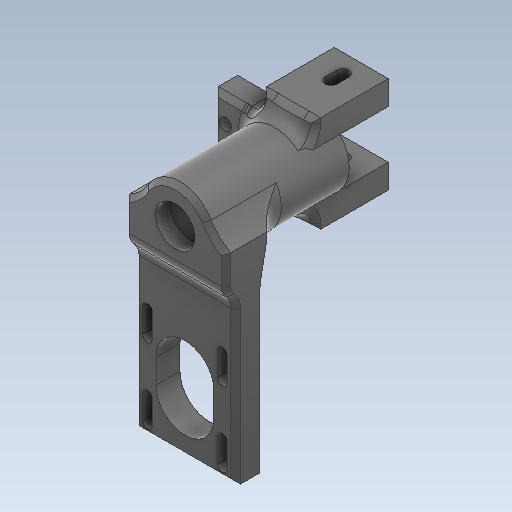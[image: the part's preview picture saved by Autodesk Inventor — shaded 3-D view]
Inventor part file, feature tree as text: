
AUTODESK INVENTOR PART (.ipt)
format: ipt  version: 2020 (Build 240168000, 168)  size: 693,760 bytes
history: native  units: mm
features: extrude x8, sketch x6, fillet x4, chamfer x4, direct_edit x2, projected_geometry x2, move_body x2, hole x1, mirror x1
ambient origin geometry x8: Origin, YZ Plane, XZ Plane, XY Plane, X Axis, Y Axis, Z Axis, Center Point
bodies: Solid1 (feature_tree)
feature tree (30):
  extrude  "Extrusion1"  Depth=57.0mm TaperAngle=0.0deg
  extrude  "Extrusion2"  Depth=5.2mm TaperAngle=0.0deg
  extrude  "Extrusion3"  Depth=10.0mm
  extrude  "Extrusion5"  Depth=20.0mm
  hole  "Hole1"  [1 undecoded]
  direct_edit  "Direct Edit1"
  fillet  "Fillet1"  Radius=5.0mm
  chamfer  "Chamfer1"  [1 undecoded]
  extrude  "Extrusion6"  Depth=10.0mm
  extrude  "Extrusion7"  Depth=10.0mm
  chamfer  "Chamfer2"  Distance=2.0mm Angle=45.0deg
  fillet  "Fillet2"  Radius=42.0mm
  fillet  "Fillet3"  Radius=65.0mm
  extrude  "Extrusion8"  Depth=10.0mm TaperAngle=0.0deg
  chamfer  "Chamfer3"  Distance=4.0mm
  extrude  "Extrusion9"  TaperAngle=0.0deg  [1 undecoded]
  fillet  "Fillet4"  Radius=4.0mm
  chamfer  "Chamfer4"  Distance=7.0mm
  direct_edit  "Direct Edit2"
  mirror  "Mirror2"
  sketch  "Sketch1"  dims[d0=30.0mm d1=57.0mm d2=0.0mm]
  sketch  "Sketch2"  dims[d3=16.3mm d4=5.2mm d5=0.0mm]
  sketch  "Sketch3"  dims[d8=10.0mm d9=10.0mm]
  sketch  "Sketch8"  dims[d10=40.0mm d11=0.0mm d16=20.0mm]
  projected_geometry  "Projected Loop4"
  sketch  "Sketch9"  dims[d17=17.0mm d18=10.0mm d19=0.0mm d20=5.0mm]
  projected_geometry  "Projected Loop5"
  sketch  "Sketch12"  dims[d21=5.0mm d22=5.0mm d23=6.0mm d24=4.0mm d25=2.0mm d26=90.0deg d27=8.0mm d28=20.594885mm d29=0.0mm d30=0.0mm d31=-10.0mm d32=20.0mm d33=6.0mm d34=2.0mm d35=2.0mm d36=45.0deg d37=42.0mm d39=65.0mm d40=13.9mm d41=0.0mm d42=4.0mm d43=0.0mm d44=0.0mm d45=4.0mm d46=2.0mm d47=45.0deg d48=7.0mm d49=15.0mm d50=10.0mm d51=4.0mm d52=0.0mm d53=0.0mm d54=10.0mm d56=2.0mm d57=2.0mm d58=45.0deg d59=5.0mm d60=5.0mm d61=10.0mm d62=0.0mm d63=0.0mm d64=54.36068mm d65=20.0mm d66=2.0mm d67=2.0mm d68=45.0deg d69=24.0mm d70=25.0mm d71=9.5mm d72=9.5mm d73=40.5mm d74=5.5mm d75=5.5mm d76=40.5mm d77=0.0mm d78=0.0mm d79=-1.0mm d80=0.872665mm]
  move_body  "Move1"
  move_body  "Move2"
note: 3 required parameter values undecoded (feature->parameter linkage not recoverable at this tier; creation-order binding heuristic only, values carry confidence <= 0.55)
